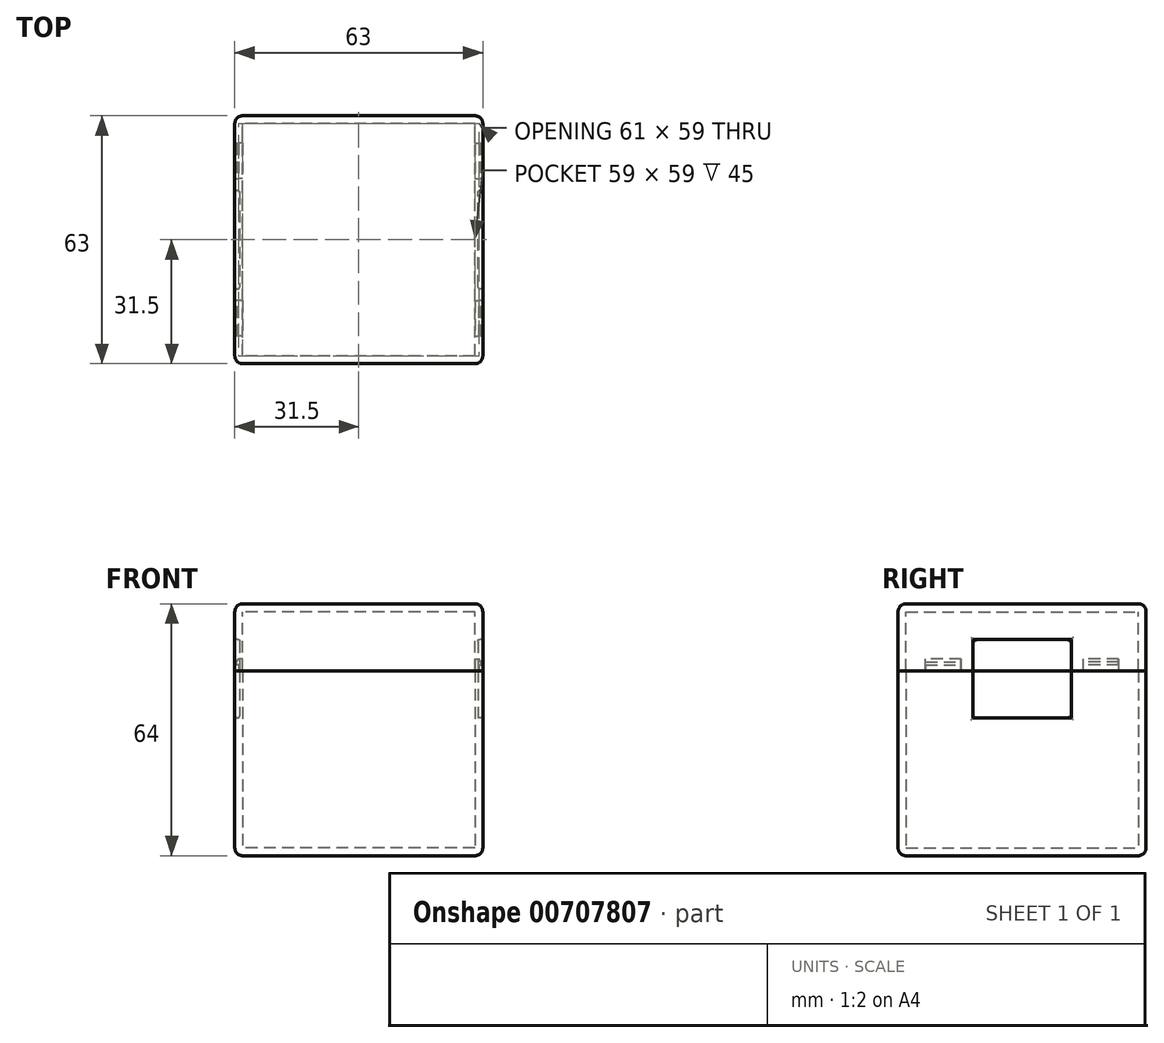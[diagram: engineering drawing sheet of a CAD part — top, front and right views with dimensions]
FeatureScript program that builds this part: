
annotation { "Feature Type Name" : "Feature", "Feature Type Description" : "" }
export const myFeature = defineFeature(function(context is Context, id is Id, definition is map)
    precondition{}
    {
        {
            assignVariable(context, id + "F0", {"name" : "Taille", "anyValue" : 56});
        }
        {
            assignVariable(context, id + "F1", {"name" : "E", "anyValue" : 2});
        }
        {
            var Q0;
            Q0=qCreatedBy(makeId("Top.planeOp"),FACE);
            var sketch = newSketch(context, id + "F2", { "sketchPlane" : qUnion([Q0])});
            skLineSegment(sketch, "E0.bottom", {"start": v(29.5, -29.5) * mm, "end": v(-29.5, -29.5) * mm});
            skLineSegment(sketch, "E0.top", {"start": v(29.5, 29.5) * mm, "end": v(-29.5, 29.5) * mm});
            skLineSegment(sketch, "E0.left", {"start": v(29.5, -29.5) * mm, "end": v(29.5, 29.5) * mm});
            skLineSegment(sketch, "E0.right", {"start": v(-29.5, -29.5) * mm, "end": v(-29.5, 29.5) * mm});
            skPoint(sketch, "E0.middle", {"position": v(0, 0) * mm});
            skLineSegment(sketch, "E1.0", {"start": v(31.5, 31.5) * mm, "end": v(-31.5, 31.5) * mm});
            skLineSegment(sketch, "E1.1", {"start": v(31.5, -31.5) * mm, "end": v(31.5, 31.5) * mm});
            skLineSegment(sketch, "E1.2", {"start": v(31.5, -31.5) * mm, "end": v(-31.5, -31.5) * mm});
            skLineSegment(sketch, "E1.3", {"start": v(-31.5, -31.5) * mm, "end": v(-31.5, 31.5) * mm});
            skSolve(sketch);
        }
        {
            var Q0;
            Q0=makeQuery(id+"F2.imprint","IMPRINT",FACE,{"disambiguationData":[TD([[makeQuery(id+"F2.imprint","IMPRINT",EDGE,{"derivedFrom":sQuery(id+"F2.wireOp",EDGE,"E0.bottom")}),1.0]])]});
            extrude(context, id + "F3", {"entities" : qUnion([Q0]), "depth" : 45 * mm, "offsetDistance" : 25 * mm});
        }
        {
            var Q0;
            Q0=makeQuery(id+"F2.imprint","IMPRINT",FACE,{"disambiguationData":[TD([[makeQuery(id+"F2.imprint","IMPRINT",EDGE,{"derivedFrom":sQuery(id+"F2.wireOp",EDGE,"E0.bottom")}),-1.0]])]});
            var Q1;
            Q1=makeQuery(id+"F2.imprint","IMPRINT",FACE,{"disambiguationData":[TD([[makeQuery(id+"F2.imprint","IMPRINT",EDGE,{"derivedFrom":sQuery(id+"F2.wireOp",EDGE,"E0.bottom")}),1.0]])]});
            extrude(context, id + "F4", {"entities" : qUnion([Q0, Q1]), "operationType" : NewBodyOperationType.ADD, "oppositeDirection" : true, "depth" : (getVariable(context, 'E')) * mm, "offsetDistance" : 25 * mm});
        }
        {
            var Q0;
            Q0=makeQuery(id+"F3.opExtrude","CAP_FACE",FACE,{"disambiguationData":[OSD([sQuery(id+"F2.wireOp",EDGE,"E0.bottom"),sQuery(id+"F2.wireOp",EDGE,"E0.top"),sQuery(id+"F2.wireOp",EDGE,"E0.left"),sQuery(id+"F2.wireOp",EDGE,"E0.right"),sQuery(id+"F2.wireOp",EDGE,"E1.0"),sQuery(id+"F2.wireOp",EDGE,"E1.1"),sQuery(id+"F2.wireOp",EDGE,"E1.2"),sQuery(id+"F2.wireOp",EDGE,"E1.3")])],"isStart":false});
            var sketch = newSketch(context, id + "F5", { "sketchPlane" : qUnion([Q0])});
            skLineSegment(sketch, "E2.bottom", {"start": v(-29.5, 24.5) * mm, "end": v(-30.5, 24.5) * mm});
            skLineSegment(sketch, "E2.top", {"start": v(-29.5, 15.5) * mm, "end": v(-30.5, 15.5) * mm});
            skLineSegment(sketch, "E2.left", {"start": v(-29.5, 24.5) * mm, "end": v(-29.5, 15.5) * mm});
            skLineSegment(sketch, "E2.right", {"start": v(-30.5, 24.5) * mm, "end": v(-30.5, 15.5) * mm});
            skSolve(sketch);
        }
        {
            var Q0;
            Q0=makeQuery(id+"F5.imprint","IMPRINT",FACE,{"disambiguationData":[TD([[makeQuery(id+"F5.imprint","IMPRINT",EDGE,{"derivedFrom":sQuery(id+"F5.wireOp",EDGE,"E2.bottom")}),1.0]])]});
            extrude(context, id + "F6", {"entities" : qUnion([Q0]), "depth" : 3 * mm, "offsetDistance" : 25 * mm});
        }
        {
            var Q0;
            Q0=makeQuery(id+"F6.opExtrude","SWEPT_FACE",FACE,{"disambiguationData":[OSD([sQuery(id+"F5.wireOp",EDGE,"E2.top")])]});
            var sketch = newSketch(context, id + "F7", { "sketchPlane" : qUnion([Q0])});
            skLineSegment(sketch, "E3", {"start": v(-30.5, 48) * mm, "end": v(-31, 47.2) * mm});
            skLineSegment(sketch, "E4", {"start": v(-31, 47.2) * mm, "end": v(-31, 46.5) * mm});
            skLineSegment(sketch, "E5", {"start": v(-31, 46.5) * mm, "end": v(-30.5, 46.5) * mm});
            skLineSegment(sketch, "E6", {"start": v(-30.5, 46.5) * mm, "end": v(-30.5, 48) * mm});
            skSolve(sketch);
        }
        {
            var Q0;
            Q0=makeQuery(id+"F7.imprint","IMPRINT",FACE,{"disambiguationData":[TD([[makeQuery(id+"F7.imprint","IMPRINT",EDGE,{"derivedFrom":sQuery(id+"F7.wireOp",EDGE,"E3")}),1.0]])]});
            var Q1;
            Q1=makeQuery(id+"F6.opExtrude","SWEPT_FACE",FACE,{"disambiguationData":[OSD([sQuery(id+"F5.wireOp",EDGE,"E2.bottom")])]});
            extrude(context, id + "F8", {"entities" : qUnion([Q0]), "operationType" : NewBodyOperationType.ADD, "endBound" : BoundingType.UP_TO_SURFACE, "oppositeDirection" : true, "depth" : 25 * mm, "endBoundEntityFace" : qUnion([Q1]), "offsetDistance" : 25 * mm});
        }
        {
            var Q0;
            Q0=makeQuery(id+"F6.opExtrude","SWEPT_BODY",BODY,{"disambiguationData":[OSD([sQuery(id+"F5.wireOp",EDGE,"E2.bottom"),sQuery(id+"F5.wireOp",EDGE,"E2.top"),sQuery(id+"F5.wireOp",EDGE,"E2.left"),sQuery(id+"F5.wireOp",EDGE,"E2.right")])]});
            var Q1;
            Q1=qCreatedBy(makeId("Right.planeOp"),FACE);
            mirror(context, id + "F9", {"operationType" : NewBodyOperationType.ADD, "entities" : qUnion([Q0]), "mirrorPlane" : qUnion([Q1])});
        }
        {
            var Q0;
            Q0=makeQuery(id+"F3.opExtrude","SWEPT_BODY",BODY,{"disambiguationData":[OSD([sQuery(id+"F2.wireOp",EDGE,"E0.bottom"),sQuery(id+"F2.wireOp",EDGE,"E0.top"),sQuery(id+"F2.wireOp",EDGE,"E0.left"),sQuery(id+"F2.wireOp",EDGE,"E0.right"),sQuery(id+"F2.wireOp",EDGE,"E1.0"),sQuery(id+"F2.wireOp",EDGE,"E1.1"),sQuery(id+"F2.wireOp",EDGE,"E1.2"),sQuery(id+"F2.wireOp",EDGE,"E1.3")])]});
            var Q1;
            Q1=qCreatedBy(makeId("Front.planeOp"),FACE);
            mirror(context, id + "F10", {"operationType" : NewBodyOperationType.ADD, "entities" : qUnion([Q0]), "mirrorPlane" : qUnion([Q1])});
        }
        {
            var Q0;
            Q0=qCreatedBy(makeId("Top.planeOp"),FACE);
            cPlane(context, id + "F11", {"entities" : qUnion([Q0]), "cplaneType" : CPlaneType.OFFSET, "offset" : (getVariable(context, 'Taille') + 2 * getVariable(context, 'E')) * mm, "width" : 150 * mm, "height" : 150 * mm});
        }
        {
            var Q0;
            Q0=qCreatedBy(id+"F11.planeOp",FACE);
            var sketch = newSketch(context, id + "F12", { "sketchPlane" : qUnion([Q0])});
            skLineSegment(sketch, "E7.0", {"start": v(31.5, -31.5) * mm, "end": v(-31.5, -31.5) * mm});
            skLineSegment(sketch, "E8.0", {"start": v(31.5, -31.5) * mm, "end": v(31.5, 31.5) * mm});
            skLineSegment(sketch, "E9.0", {"start": v(29.5, -29.5) * mm, "end": v(29.5, 29.5) * mm});
            skLineSegment(sketch, "E10.0", {"start": v(29.5, -29.5) * mm, "end": v(-29.5, -29.5) * mm});
            skLineSegment(sketch, "E11.0", {"start": v(-29.5, -29.5) * mm, "end": v(-29.5, 29.5) * mm});
            skLineSegment(sketch, "E12.0", {"start": v(-31.5, -31.5) * mm, "end": v(-31.5, 31.5) * mm});
            skLineSegment(sketch, "E13.0", {"start": v(29.5, 29.5) * mm, "end": v(-29.5, 29.5) * mm});
            skLineSegment(sketch, "E14.0", {"start": v(31.5, 31.5) * mm, "end": v(-31.5, 31.5) * mm});
            skSolve(sketch);
        }
        {
            var Q0;
            Q0=makeQuery(id+"F12.imprint","IMPRINT",FACE,{"disambiguationData":[TD([[makeQuery(id+"F12.imprint","IMPRINT",EDGE,{"derivedFrom":sQuery(id+"F12.wireOp",EDGE,"E7.0")}),-1.0]])]});
            extrude(context, id + "F13", {"entities" : qUnion([Q0]), "endBound" : BoundingType.UP_TO_NEXT, "oppositeDirection" : true, "depth" : 25 * mm, "offsetDistance" : 25 * mm});
        }
        {
            var Q0;
            Q0=makeQuery(id+"F12.imprint","IMPRINT",FACE,{"disambiguationData":[TD([[makeQuery(id+"F12.imprint","IMPRINT",EDGE,{"derivedFrom":sQuery(id+"F12.wireOp",EDGE,"E9.0")}),1.0]])]});
            var Q1;
            Q1=makeQuery(id+"F12.imprint","IMPRINT",FACE,{"disambiguationData":[TD([[makeQuery(id+"F12.imprint","IMPRINT",EDGE,{"derivedFrom":sQuery(id+"F12.wireOp",EDGE,"E7.0")}),-1.0]])]});
            extrude(context, id + "F14", {"entities" : qUnion([Q0, Q1]), "operationType" : NewBodyOperationType.ADD, "depth" : (getVariable(context, 'E')) * mm, "offsetDistance" : 25 * mm});
        }
        {
            var Q0;
            Q0=makeQuery(id+"F14.opExtrude","CAP_EDGE",EDGE,{"disambiguationData":[OSD([sQuery(id+"F12.wireOp",EDGE,"E14.0")])],"isStart":false});
            var Q1;
            Q1=makeQuery(id+"F14.opExtrude","CAP_EDGE",EDGE,{"disambiguationData":[OSD([sQuery(id+"F12.wireOp",EDGE,"E12.0")])],"isStart":false});
            var Q2;
            Q2=makeQuery(id+"F14.opExtrude","CAP_EDGE",EDGE,{"disambiguationData":[OSD([sQuery(id+"F12.wireOp",EDGE,"E7.0")])],"isStart":false});
            var Q3;
            Q3=makeQuery(id+"F14.opExtrude","CAP_EDGE",EDGE,{"disambiguationData":[OSD([sQuery(id+"F12.wireOp",EDGE,"E8.0")])],"isStart":false});
            var Q4;
            {var subQ0=sQuery(id+"F12.wireOp",EDGE,"E14.0");var subQ1=sQuery(id+"F12.wireOp",EDGE,"E12.0");Q4=makeQuery(id+"F14.boolean.opBoolean","MERGE",EDGE,{"derivedFrom":[makeQuery(id+"F13.opExtrude","SWEPT_EDGE",EDGE,{"disambiguationData":[OSD([subQ1,subQ0])]}),makeQuery(id+"F14.opExtrude","SWEPT_EDGE",EDGE,{"disambiguationData":[OSD([subQ1,subQ0])]})]});}
            var Q5;
            {var subQ0=sQuery(id+"F2.wireOp",EDGE,"E1.3");var subQ1=sQuery(id+"F2.wireOp",EDGE,"E1.0");Q5=makeQuery(id+"F4.boolean.opBoolean","MERGE",EDGE,{"derivedFrom":[makeQuery(id+"F3.opExtrude","SWEPT_EDGE",EDGE,{"disambiguationData":[OSD([subQ1,subQ0])]}),makeQuery(id+"F4.opExtrude","SWEPT_EDGE",EDGE,{"disambiguationData":[OSD([subQ1,subQ0])]})]});}
            var Q6;
            {var subQ0=sQuery(id+"F2.wireOp",EDGE,"E1.1");var subQ1=sQuery(id+"F2.wireOp",EDGE,"E1.0");Q6=makeQuery(id+"F4.boolean.opBoolean","MERGE",EDGE,{"derivedFrom":[makeQuery(id+"F3.opExtrude","SWEPT_EDGE",EDGE,{"disambiguationData":[OSD([subQ1,subQ0])]}),makeQuery(id+"F4.opExtrude","SWEPT_EDGE",EDGE,{"disambiguationData":[OSD([subQ1,subQ0])]})]});}
            var Q7;
            Q7=makeQuery(id+"F14.boolean.opBoolean","MERGE",EDGE,{"derivedFrom":[makeQuery(id+"F13.opExtrude","SWEPT_EDGE",EDGE,{"disambiguationData":[OSD([sQuery(id+"F2.wireOp",EDGE,"E1.0"),sQuery(id+"F2.wireOp",EDGE,"E1.1")])]}),makeQuery(id+"F14.opExtrude","SWEPT_EDGE",EDGE,{"disambiguationData":[OSD([sQuery(id+"F12.wireOp",EDGE,"E8.0"),sQuery(id+"F12.wireOp",EDGE,"E14.0")])]})]});
            var Q8;
            {var subQ0=sQuery(id+"F12.wireOp",EDGE,"E12.0");var subQ1=sQuery(id+"F12.wireOp",EDGE,"E7.0");Q8=makeQuery(id+"F14.boolean.opBoolean","MERGE",EDGE,{"derivedFrom":[makeQuery(id+"F13.opExtrude","SWEPT_EDGE",EDGE,{"disambiguationData":[OSD([subQ1,subQ0])]}),makeQuery(id+"F14.opExtrude","SWEPT_EDGE",EDGE,{"disambiguationData":[OSD([subQ1,subQ0])]})]});}
            var Q9;
            {var subQ0=sQuery(id+"F2.wireOp",EDGE,"E1.3");var subQ1=sQuery(id+"F2.wireOp",EDGE,"E1.2");Q9=makeQuery(id+"F4.boolean.opBoolean","MERGE",EDGE,{"derivedFrom":[makeQuery(id+"F3.opExtrude","SWEPT_EDGE",EDGE,{"disambiguationData":[OSD([subQ1,subQ0])]}),makeQuery(id+"F4.opExtrude","SWEPT_EDGE",EDGE,{"disambiguationData":[OSD([subQ1,subQ0])]})]});}
            var Q10;
            {var subQ0=sQuery(id+"F2.wireOp",EDGE,"E1.2");var subQ1=sQuery(id+"F2.wireOp",EDGE,"E1.1");Q10=makeQuery(id+"F4.boolean.opBoolean","MERGE",EDGE,{"derivedFrom":[makeQuery(id+"F3.opExtrude","SWEPT_EDGE",EDGE,{"disambiguationData":[OSD([subQ1,subQ0])]}),makeQuery(id+"F4.opExtrude","SWEPT_EDGE",EDGE,{"disambiguationData":[OSD([subQ1,subQ0])]})]});}
            var Q11;
            {var subQ0=sQuery(id+"F12.wireOp",EDGE,"E8.0");var subQ1=sQuery(id+"F12.wireOp",EDGE,"E7.0");Q11=makeQuery(id+"F14.boolean.opBoolean","MERGE",EDGE,{"derivedFrom":[makeQuery(id+"F13.opExtrude","SWEPT_EDGE",EDGE,{"disambiguationData":[OSD([subQ1,subQ0])]}),makeQuery(id+"F14.opExtrude","SWEPT_EDGE",EDGE,{"disambiguationData":[OSD([subQ1,subQ0])]})]});}
            var Q12;
            Q12=makeQuery(id+"F4.opExtrude","CAP_EDGE",EDGE,{"disambiguationData":[OSD([sQuery(id+"F2.wireOp",EDGE,"E1.1")])],"isStart":false});
            var Q13;
            Q13=makeQuery(id+"F4.opExtrude","CAP_EDGE",EDGE,{"disambiguationData":[OSD([sQuery(id+"F2.wireOp",EDGE,"E1.2")])],"isStart":false});
            var Q14;
            Q14=makeQuery(id+"F4.opExtrude","CAP_EDGE",EDGE,{"disambiguationData":[OSD([sQuery(id+"F2.wireOp",EDGE,"E1.0")])],"isStart":false});
            var Q15;
            Q15=makeQuery(id+"F4.opExtrude","CAP_EDGE",EDGE,{"disambiguationData":[OSD([sQuery(id+"F2.wireOp",EDGE,"E1.3")])],"isStart":false});
            fillet(context, id + "F15", {"entities" : qUnion([Q0, Q1, Q2, Q3, Q4, Q5, Q6, Q7, Q8, Q9, Q10, Q11, Q12, Q13, Q14, Q15]), "radius" : 2 * mm, "tangentPropagation" : true, "allowEdgeOverflow" : false});
        }
        {
            var Q0;
            {var subQ0=sQuery(id+"F12.wireOp",EDGE,"E8.0");Q0=makeQuery(id+"F14.boolean.opBoolean","MERGE",FACE,{"derivedFrom":[makeQuery(id+"F13.opExtrude","SWEPT_FACE",FACE,{"disambiguationData":[OSD([subQ0])]}),makeQuery(id+"F14.opExtrude","SWEPT_FACE",FACE,{"disambiguationData":[OSD([subQ0])]})]});}
            var sketch = newSketch(context, id + "F16", { "sketchPlane" : qUnion([Q0])});
            skLineSegment(sketch, "E15.bottom", {"start": v(12.5, 53) * mm, "end": v(-12.5, 53) * mm});
            skLineSegment(sketch, "E15.top", {"start": v(12.5, 33) * mm, "end": v(-12.5, 33) * mm});
            skLineSegment(sketch, "E15.left", {"start": v(12.5, 53) * mm, "end": v(12.5, 33) * mm});
            skLineSegment(sketch, "E15.right", {"start": v(-12.5, 53) * mm, "end": v(-12.5, 33) * mm});
            skSolve(sketch);
        }
        {
            var Q0;
            {var subQ0=sQuery(id+"F12.wireOp",EDGE,"E12.0");Q0=makeQuery(id+"F14.boolean.opBoolean","MERGE",FACE,{"derivedFrom":[makeQuery(id+"F13.opExtrude","SWEPT_FACE",FACE,{"disambiguationData":[OSD([subQ0])]}),makeQuery(id+"F14.opExtrude","SWEPT_FACE",FACE,{"disambiguationData":[OSD([subQ0])]})]});}
            var sketch = newSketch(context, id + "F17", { "sketchPlane" : qUnion([Q0])});
            skLineSegment(sketch, "E16.bottom", {"start": v(12.5, 53) * mm, "end": v(-12.5, 53) * mm});
            skLineSegment(sketch, "E16.top", {"start": v(12.5, 33) * mm, "end": v(-12.5, 33) * mm});
            skLineSegment(sketch, "E16.left", {"start": v(12.5, 53) * mm, "end": v(12.5, 33) * mm});
            skLineSegment(sketch, "E16.right", {"start": v(-12.5, 53) * mm, "end": v(-12.5, 33) * mm});
            skSolve(sketch);
        }
        {
            var Q0;
            {var subQ0=sQuery(id+"F17.wireOp",EDGE,"E16.bottom");Q0=makeQuery(id+"F17.imprint","IMPRINT",FACE,{"disambiguationData":[TD([[makeQuery(id+"F17.imprint","IMPRINT",EDGE,{"derivedFrom":subQ0}),1.0]])]});}
            var Q1;
            {var subQ0=sQuery(id+"F17.wireOp",EDGE,"E16.top");Q1=makeQuery(id+"F17.imprint","IMPRINT",FACE,{"disambiguationData":[TD([[makeQuery(id+"F17.imprint","IMPRINT",EDGE,{"derivedFrom":subQ0}),-1.0]])]});}
            var Q2;
            {var subQ0=sQuery(id+"F16.wireOp",EDGE,"E15.bottom");Q2=makeQuery(id+"F16.imprint","IMPRINT",FACE,{"disambiguationData":[TD([[makeQuery(id+"F16.imprint","IMPRINT",EDGE,{"derivedFrom":subQ0}),1.0]])]});}
            var Q3;
            {var subQ0=sQuery(id+"F16.wireOp",EDGE,"E15.top");Q3=makeQuery(id+"F16.imprint","IMPRINT",FACE,{"disambiguationData":[TD([[makeQuery(id+"F16.imprint","IMPRINT",EDGE,{"derivedFrom":subQ0}),-1.0]])]});}
            extrude(context, id + "F18", {"entities" : qUnion([Q0, Q1, Q2, Q3]), "operationType" : NewBodyOperationType.REMOVE, "endBound" : BoundingType.SYMMETRIC, "oppositeDirection" : true, "depth" : 2.5 * mm, "offsetDistance" : 25 * mm});
        }
        {
            var Q0;
            Q0=makeQuery(id+"F18.boolean.opBoolean","COPY",EDGE,{"derivedFrom":makeQuery(id+"F18.opExtrude","CAP_EDGE",EDGE,{"disambiguationData":[OSD([sQuery(id+"F16.wireOp",EDGE,"E15.bottom")])],"isStart":false})});
            var Q1;
            Q1=makeQuery(id+"F18.boolean.opBoolean","COPY",EDGE,{"derivedFrom":makeQuery(id+"F18.opExtrude","CAP_EDGE",EDGE,{"disambiguationData":[OSD([sQuery(id+"F16.wireOp",EDGE,"E15.right")])],"isStart":false})});
            var Q2;
            Q2=makeQuery(id+"F18.boolean.opBoolean","COPY",EDGE,{"derivedFrom":makeQuery(id+"F18.opExtrude","CAP_EDGE",EDGE,{"disambiguationData":[OSD([sQuery(id+"F16.wireOp",EDGE,"E15.left")])],"isStart":false})});
            var Q3;
            Q3=makeQuery(id+"F18.boolean.opBoolean","COPY",EDGE,{"derivedFrom":makeQuery(id+"F18.opExtrude","CAP_EDGE",EDGE,{"disambiguationData":[OSD([sQuery(id+"F16.wireOp",EDGE,"E15.left")])],"isStart":true})});
            var Q4;
            Q4=makeQuery(id+"F18.boolean.opBoolean","COPY",EDGE,{"derivedFrom":makeQuery(id+"F18.opExtrude","CAP_EDGE",EDGE,{"disambiguationData":[OSD([sQuery(id+"F16.wireOp",EDGE,"E15.bottom")])],"isStart":true})});
            var Q5;
            Q5=makeQuery(id+"F18.boolean.opBoolean","COPY",EDGE,{"derivedFrom":makeQuery(id+"F18.opExtrude","CAP_EDGE",EDGE,{"disambiguationData":[OSD([sQuery(id+"F16.wireOp",EDGE,"E15.right")])],"isStart":true})});
            var Q6;
            Q6=makeQuery(id+"F18.boolean.opBoolean","COPY",EDGE,{"derivedFrom":makeQuery(id+"F18.opExtrude","CAP_EDGE",EDGE,{"disambiguationData":[OSD([sQuery(id+"F17.wireOp",EDGE,"E16.bottom")])],"isStart":false})});
            var Q7;
            {var subQ0=sQuery(id+"F12.wireOp",EDGE,"E12.0");Q7=makeQuery(id+"F18.boolean.opBoolean","INTERSECT",EDGE,{"derivedFrom":[makeQuery(id+"F14.boolean.opBoolean","MERGE",FACE,{"derivedFrom":[makeQuery(id+"F13.opExtrude","SWEPT_FACE",FACE,{"disambiguationData":[OSD([subQ0])]}),makeQuery(id+"F14.opExtrude","SWEPT_FACE",FACE,{"disambiguationData":[OSD([subQ0])]})]}),makeQuery(id+"F18.opExtrude","SWEPT_FACE",FACE,{"disambiguationData":[OSD([sQuery(id+"F17.wireOp",EDGE,"E16.left")])]})]});}
            var Q8;
            {var subQ0=sQuery(id+"F2.wireOp",EDGE,"E1.3");Q8=makeQuery(id+"F18.boolean.opBoolean","INTERSECT",EDGE,{"derivedFrom":[makeQuery(id+"F4.boolean.opBoolean","MERGE",FACE,{"derivedFrom":[makeQuery(id+"F3.opExtrude","SWEPT_FACE",FACE,{"disambiguationData":[OSD([subQ0])]}),makeQuery(id+"F4.opExtrude","SWEPT_FACE",FACE,{"disambiguationData":[OSD([subQ0])]})]}),makeQuery(id+"F18.opExtrude","SWEPT_FACE",FACE,{"disambiguationData":[OSD([sQuery(id+"F17.wireOp",EDGE,"E16.left")])]})]});}
            var Q9;
            {var subQ0=sQuery(id+"F2.wireOp",EDGE,"E1.3");Q9=makeQuery(id+"F18.boolean.opBoolean","INTERSECT",EDGE,{"derivedFrom":[makeQuery(id+"F4.boolean.opBoolean","MERGE",FACE,{"derivedFrom":[makeQuery(id+"F3.opExtrude","SWEPT_FACE",FACE,{"disambiguationData":[OSD([subQ0])]}),makeQuery(id+"F4.opExtrude","SWEPT_FACE",FACE,{"disambiguationData":[OSD([subQ0])]})]}),makeQuery(id+"F18.opExtrude","SWEPT_FACE",FACE,{"disambiguationData":[OSD([sQuery(id+"F17.wireOp",EDGE,"E16.top")])]})]});}
            var Q10;
            {var subQ0=sQuery(id+"F2.wireOp",EDGE,"E1.3");Q10=makeQuery(id+"F18.boolean.opBoolean","INTERSECT",EDGE,{"derivedFrom":[makeQuery(id+"F4.boolean.opBoolean","MERGE",FACE,{"derivedFrom":[makeQuery(id+"F3.opExtrude","SWEPT_FACE",FACE,{"disambiguationData":[OSD([subQ0])]}),makeQuery(id+"F4.opExtrude","SWEPT_FACE",FACE,{"disambiguationData":[OSD([subQ0])]})]}),makeQuery(id+"F18.opExtrude","SWEPT_FACE",FACE,{"disambiguationData":[OSD([sQuery(id+"F17.wireOp",EDGE,"E16.right")])]})]});}
            var Q11;
            {var subQ0=sQuery(id+"F12.wireOp",EDGE,"E12.0");Q11=makeQuery(id+"F18.boolean.opBoolean","INTERSECT",EDGE,{"derivedFrom":[makeQuery(id+"F14.boolean.opBoolean","MERGE",FACE,{"derivedFrom":[makeQuery(id+"F13.opExtrude","SWEPT_FACE",FACE,{"disambiguationData":[OSD([subQ0])]}),makeQuery(id+"F14.opExtrude","SWEPT_FACE",FACE,{"disambiguationData":[OSD([subQ0])]})]}),makeQuery(id+"F18.opExtrude","SWEPT_FACE",FACE,{"disambiguationData":[OSD([sQuery(id+"F17.wireOp",EDGE,"E16.right")])]})]});}
            var Q12;
            {var subQ0=sQuery(id+"F12.wireOp",EDGE,"E12.0");Q12=makeQuery(id+"F18.boolean.opBoolean","INTERSECT",EDGE,{"derivedFrom":[makeQuery(id+"F14.boolean.opBoolean","MERGE",FACE,{"derivedFrom":[makeQuery(id+"F13.opExtrude","SWEPT_FACE",FACE,{"disambiguationData":[OSD([subQ0])]}),makeQuery(id+"F14.opExtrude","SWEPT_FACE",FACE,{"disambiguationData":[OSD([subQ0])]})]}),makeQuery(id+"F18.opExtrude","SWEPT_FACE",FACE,{"disambiguationData":[OSD([sQuery(id+"F17.wireOp",EDGE,"E16.bottom")])]})]});}
            var Q13;
            {var subQ0=sQuery(id+"F17.wireOp",EDGE,"E16.bottom");var subQ1=sQuery(id+"F17.wireOp",EDGE,"E16.right");Q13=makeQuery(id+"F18.boolean.opBoolean","COPY",EDGE,{"disambiguationData":[TD([makeQuery(id+"F18.opExtrude","SWEPT_FACE",FACE,{"disambiguationData":[OSD([subQ0])]})])],"derivedFrom":makeQuery(id+"F18.opExtrude","CAP_EDGE",EDGE,{"disambiguationData":[OSD([subQ1])],"isStart":false})});}
            var Q14;
            {var subQ0=sQuery(id+"F17.wireOp",EDGE,"E16.right");var subQ1=sQuery(id+"F17.wireOp",EDGE,"E16.top");Q14=makeQuery(id+"F18.boolean.opBoolean","COPY",EDGE,{"disambiguationData":[TD([makeQuery(id+"F18.opExtrude","SWEPT_FACE",FACE,{"disambiguationData":[OSD([subQ1])]})])],"derivedFrom":makeQuery(id+"F18.opExtrude","CAP_EDGE",EDGE,{"disambiguationData":[OSD([subQ0])],"isStart":false})});}
            var Q15;
            Q15=makeQuery(id+"F18.boolean.opBoolean","COPY",EDGE,{"derivedFrom":makeQuery(id+"F18.opExtrude","CAP_EDGE",EDGE,{"disambiguationData":[OSD([sQuery(id+"F17.wireOp",EDGE,"E16.top")])],"isStart":false})});
            var Q16;
            {var subQ0=sQuery(id+"F17.wireOp",EDGE,"E16.bottom");var subQ1=sQuery(id+"F17.wireOp",EDGE,"E16.left");Q16=makeQuery(id+"F18.boolean.opBoolean","COPY",EDGE,{"disambiguationData":[TD([makeQuery(id+"F18.opExtrude","SWEPT_FACE",FACE,{"disambiguationData":[OSD([subQ0])]})])],"derivedFrom":makeQuery(id+"F18.opExtrude","CAP_EDGE",EDGE,{"disambiguationData":[OSD([subQ1])],"isStart":false})});}
            var Q17;
            {var subQ0=sQuery(id+"F17.wireOp",EDGE,"E16.left");var subQ1=sQuery(id+"F17.wireOp",EDGE,"E16.top");Q17=makeQuery(id+"F18.boolean.opBoolean","COPY",EDGE,{"disambiguationData":[TD([makeQuery(id+"F18.opExtrude","SWEPT_FACE",FACE,{"disambiguationData":[OSD([subQ1])]})])],"derivedFrom":makeQuery(id+"F18.opExtrude","CAP_EDGE",EDGE,{"disambiguationData":[OSD([subQ0])],"isStart":false})});}
            fillet(context, id + "F19", {"entities" : qUnion([Q0, Q1, Q2, Q3, Q4, Q5, Q6, Q7, Q8, Q9, Q10, Q11, Q12, Q13, Q14, Q15, Q16, Q17]), "radius" : 0.5 * mm, "tangentPropagation" : true, "allowEdgeOverflow" : false});
        }
    });
